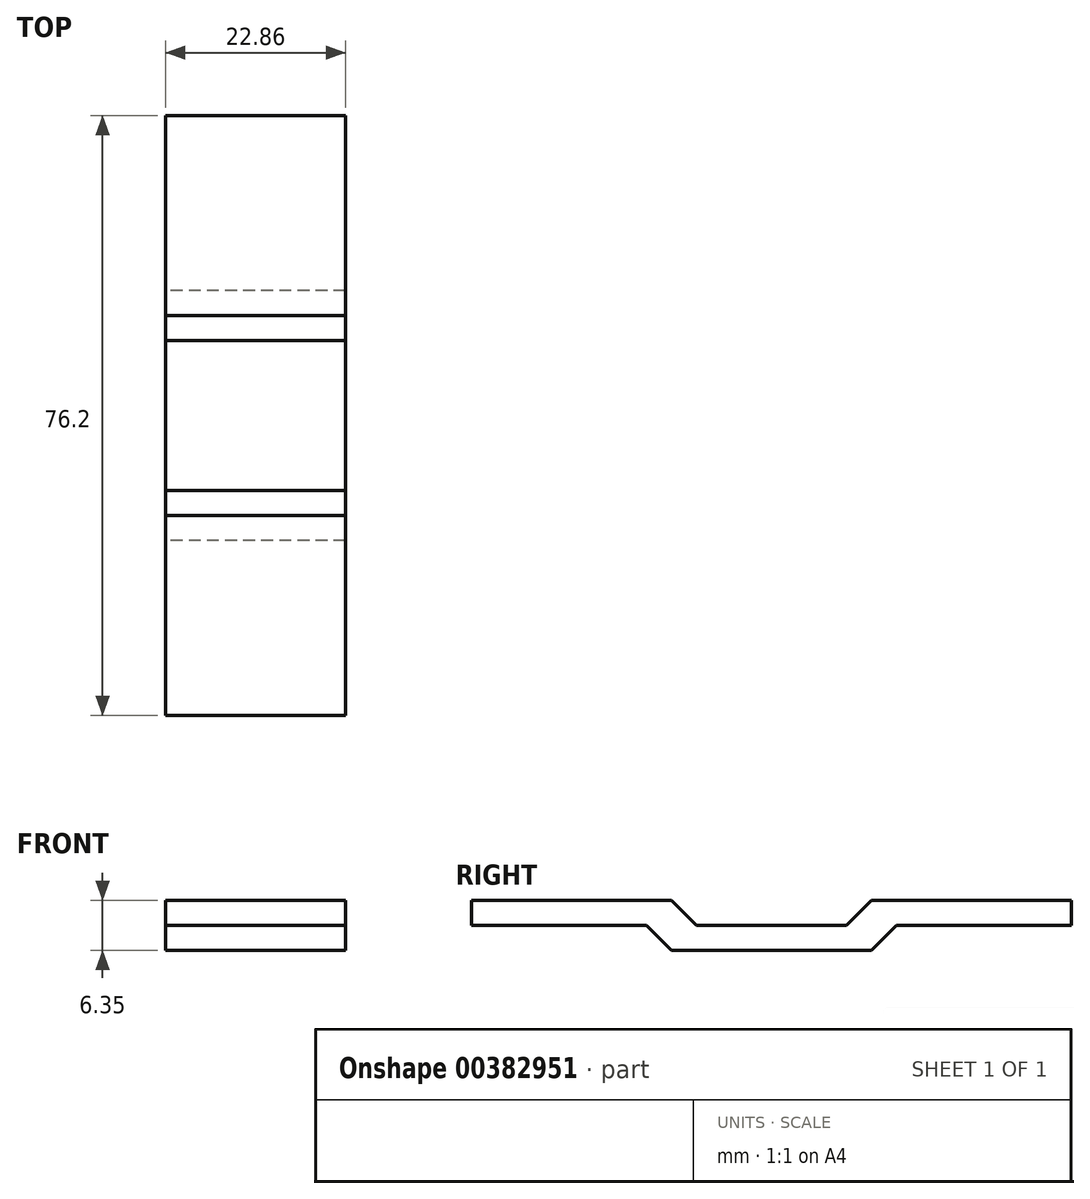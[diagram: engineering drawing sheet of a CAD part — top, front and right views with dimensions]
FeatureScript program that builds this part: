
annotation { "Feature Type Name" : "Feature", "Feature Type Description" : "" }
export const myFeature = defineFeature(function(context is Context, id is Id, definition is map)
    precondition{}
    {
        {
            var Q0;
            Q0=qCreatedBy(makeId("Right.planeOp"),FACE);
            var sketch = newSketch(context, id + "F0", { "sketchPlane" : qUnion([Q0])});
            skLineSegment(sketch, "E0.bottom", {"start": v(12.7, 1.59) * mm, "end": v(-12.7, 1.59) * mm});
            skLineSegment(sketch, "E0.top", {"start": v(12.7, -1.59) * mm, "end": v(-12.7, -1.59) * mm});
            skLineSegment(sketch, "E0.left", {"start": v(12.7, 1.59) * mm, "end": v(12.7, -1.59) * mm});
            skLineSegment(sketch, "E0.right", {"start": v(-12.7, 1.59) * mm, "end": v(-12.7, -1.59) * mm});
            skPoint(sketch, "E0.middle", {"position": v(0, 0) * mm});
            skLineSegment(sketch, "E1.bottom", {"start": v(12.7, 1.59) * mm, "end": v(38.1, 1.59) * mm});
            skLineSegment(sketch, "E1.top", {"start": v(12.7, 4.76) * mm, "end": v(38.1, 4.76) * mm});
            skLineSegment(sketch, "E1.left", {"start": v(12.7, 1.59) * mm, "end": v(12.7, 4.76) * mm});
            skLineSegment(sketch, "E1.right", {"start": v(38.1, 1.59) * mm, "end": v(38.1, 4.76) * mm});
            skLineSegment(sketch, "E2.bottom", {"start": v(-12.7, 1.59) * mm, "end": v(-38.1, 1.59) * mm});
            skLineSegment(sketch, "E2.top", {"start": v(-12.7, 4.76) * mm, "end": v(-38.1, 4.76) * mm});
            skLineSegment(sketch, "E2.left", {"start": v(-12.7, 1.59) * mm, "end": v(-12.7, 4.76) * mm});
            skLineSegment(sketch, "E2.right", {"start": v(-38.1, 1.59) * mm, "end": v(-38.1, 4.76) * mm});
            skLineSegment(sketch, "E3", {"start": v(-12.7, -1.59) * mm, "end": v(-15.88, 1.59) * mm});
            skLineSegment(sketch, "E4", {"start": v(12.7, -1.59) * mm, "end": v(15.88, 1.59) * mm});
            skLineSegment(sketch, "E5", {"start": v(-12.7, 4.76) * mm, "end": v(-9.52, 1.59) * mm});
            skLineSegment(sketch, "E6", {"start": v(12.7, 4.76) * mm, "end": v(9.53, 1.59) * mm});
            skSolve(sketch);
        }
        {
            var Q0;
            Q0=makeQuery(id+"F0.imprint","IMPRINT",FACE,{"disambiguationData":[TD([[makeQuery(id+"F0.imprint","IMPRINT",EDGE,{"derivedFrom":sQuery(id+"F0.wireOp",EDGE,"E2.top")}),1.0]])]});
            var Q1;
            {var subQ0=sQuery(id+"F0.wireOp",EDGE,"E1.left");Q1=makeQuery(id+"F0.imprint","IMPRINT",FACE,{"disambiguationData":[TD([[makeQuery(id+"F0.imprint","IMPRINT",EDGE,{"derivedFrom":subQ0}),1.0]])]});}
            var Q2;
            {var subQ0=sQuery(id+"F0.wireOp",EDGE,"E2.left");Q2=makeQuery(id+"F0.imprint","IMPRINT",FACE,{"disambiguationData":[TD([[makeQuery(id+"F0.imprint","IMPRINT",EDGE,{"derivedFrom":subQ0}),-1.0]])]});}
            var Q3;
            {var subQ0=sQuery(id+"F0.wireOp",EDGE,"E0.left");Q3=makeQuery(id+"F0.imprint","IMPRINT",FACE,{"disambiguationData":[TD([[makeQuery(id+"F0.imprint","IMPRINT",EDGE,{"derivedFrom":subQ0}),1.0]])]});}
            var Q4;
            {var subQ0=sQuery(id+"F0.wireOp",EDGE,"E0.right");Q4=makeQuery(id+"F0.imprint","IMPRINT",FACE,{"disambiguationData":[TD([[makeQuery(id+"F0.imprint","IMPRINT",EDGE,{"derivedFrom":subQ0}),-1.0]])]});}
            var Q5;
            Q5=makeQuery(id+"F0.imprint","IMPRINT",FACE,{"disambiguationData":[TD([[makeQuery(id+"F0.imprint","IMPRINT",EDGE,{"derivedFrom":sQuery(id+"F0.wireOp",EDGE,"E1.top")}),-1.0]])]});
            var Q6;
            Q6=makeQuery(id+"F0.imprint","IMPRINT",FACE,{"disambiguationData":[TD([[makeQuery(id+"F0.imprint","IMPRINT",EDGE,{"derivedFrom":sQuery(id+"F0.wireOp",EDGE,"E0.top")}),-1.0]])]});
            extrude(context, id + "F1", {"entities" : qUnion([Q0, Q1, Q2, Q3, Q4, Q5, Q6]), "endBound" : BoundingType.SYMMETRIC, "depth" : 22.86 * mm});
        }
    });
